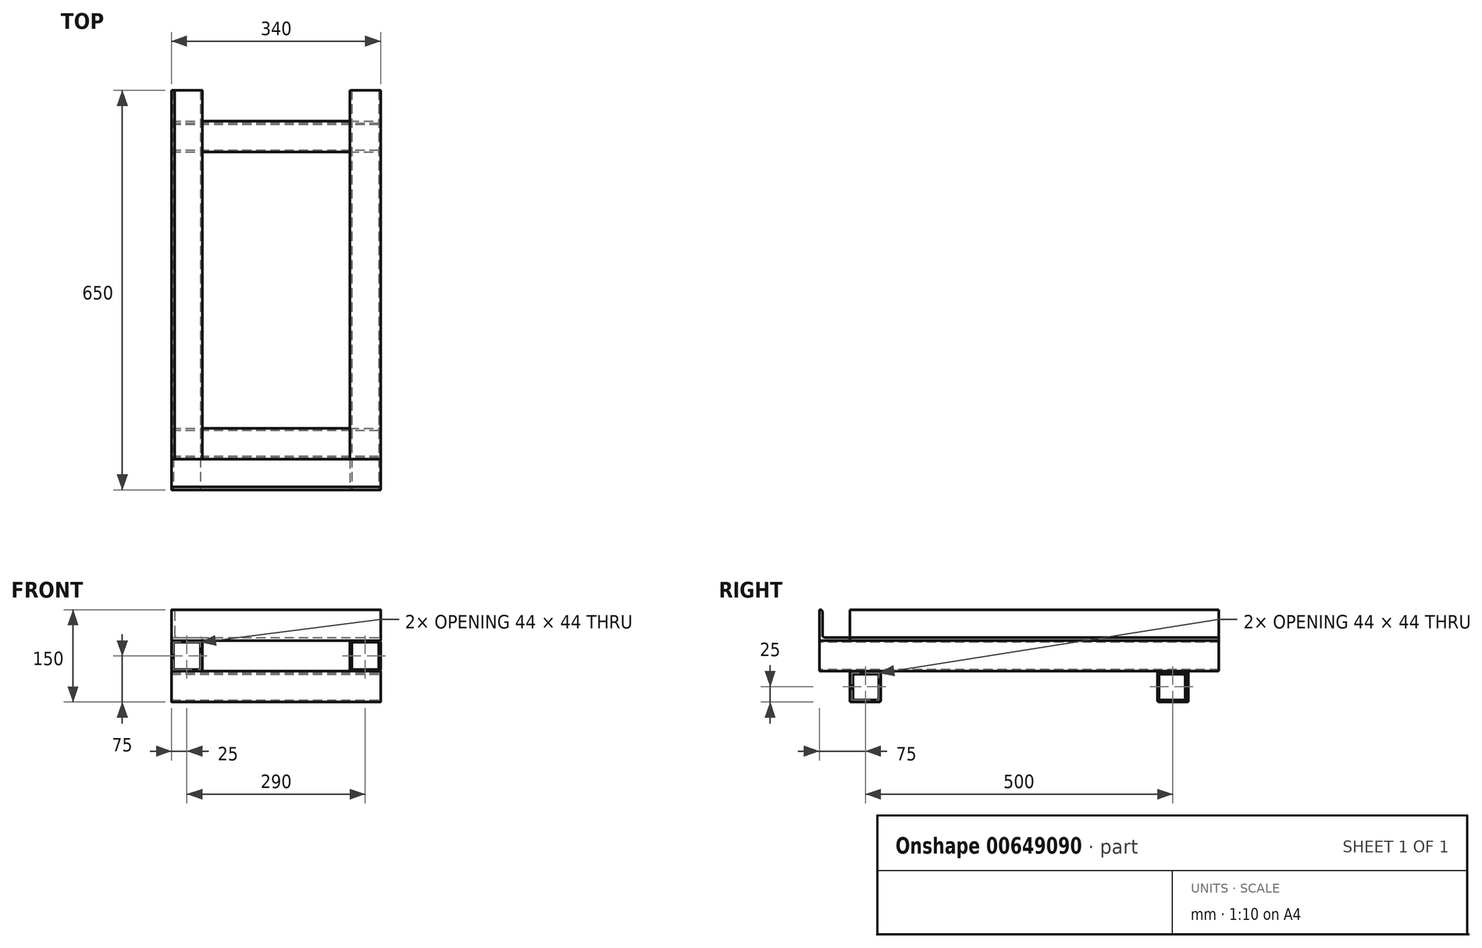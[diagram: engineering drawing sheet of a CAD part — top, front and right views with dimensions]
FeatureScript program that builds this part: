
annotation { "Feature Type Name" : "Feature", "Feature Type Description" : "" }
export const myFeature = defineFeature(function(context is Context, id is Id, definition is map)
    precondition{}
    {
        {
            var Q0;
            Q0=qCreatedBy(makeId("Front.planeOp"),FACE);
            cPlane(context, id + "F0", {"entities" : qUnion([Q0]), "cplaneType" : CPlaneType.OFFSET, "offset" : 300 * mm, "width" : 150 * mm, "height" : 150 * mm});
        }
        {
            var Q0;
            Q0=qCreatedBy(id+"F0.planeOp",FACE);
            var sketch = newSketch(context, id + "F1", { "sketchPlane" : qUnion([Q0])});
            skLineSegment(sketch, "E0.bottom", {"start": v(-167, 250) * mm, "end": v(-123, 250) * mm});
            skLineSegment(sketch, "E0.top", {"start": v(-167, 200) * mm, "end": v(-123, 200) * mm});
            skLineSegment(sketch, "E0.left", {"start": v(-170, 247) * mm, "end": v(-170, 203) * mm});
            skLineSegment(sketch, "E0.right", {"start": v(-120, 247) * mm, "end": v(-120, 203) * mm});
            skLineSegment(sketch, "E1.bottom", {"start": v(123, 250) * mm, "end": v(167, 250) * mm});
            skLineSegment(sketch, "E1.top", {"start": v(123, 200) * mm, "end": v(167, 200) * mm});
            skLineSegment(sketch, "E1.left", {"start": v(120, 247) * mm, "end": v(120, 203) * mm});
            skLineSegment(sketch, "E1.right", {"start": v(170, 247) * mm, "end": v(170, 203) * mm});
            skLineSegment(sketch, "E2.0", {"start": v(-165.5, 203) * mm, "end": v(-124.5, 203) * mm});
            skLineSegment(sketch, "E2.1", {"start": v(-167, 245.5) * mm, "end": v(-167, 204.5) * mm});
            skLineSegment(sketch, "E2.2", {"start": v(-165.5, 247) * mm, "end": v(-124.5, 247) * mm});
            skLineSegment(sketch, "E2.3", {"start": v(-123, 245.5) * mm, "end": v(-123, 204.5) * mm});
            skLineSegment(sketch, "E3.0", {"start": v(124.5, 203) * mm, "end": v(165.5, 203) * mm});
            skLineSegment(sketch, "E3.1", {"start": v(123, 245.5) * mm, "end": v(123, 204.5) * mm});
            skLineSegment(sketch, "E3.2", {"start": v(124.5, 247) * mm, "end": v(165.5, 247) * mm});
            skLineSegment(sketch, "E3.3", {"start": v(167, 245.5) * mm, "end": v(167, 204.5) * mm});
            skPoint(sketch, "E4.visualSharp", {"position": v(-170, 250) * mm});
            skArc(sketch, "E4.filletArc", {"start": v(-167, 250) * mm, "mid": v(-169.12, 249.12) * mm, "end": v(-170, 247) * mm});
            skPoint(sketch, "E5.visualSharp", {"position": v(-120, 250) * mm});
            skArc(sketch, "E5.filletArc", {"start": v(-120, 247) * mm, "mid": v(-120.88, 249.12) * mm, "end": v(-123, 250) * mm});
            skPoint(sketch, "E6.visualSharp", {"position": v(-120, 200) * mm});
            skArc(sketch, "E6.filletArc", {"start": v(-123, 200) * mm, "mid": v(-120.88, 200.88) * mm, "end": v(-120, 203) * mm});
            skPoint(sketch, "E7.visualSharp", {"position": v(-170, 200) * mm});
            skArc(sketch, "E7.filletArc", {"start": v(-170, 203) * mm, "mid": v(-169.12, 200.88) * mm, "end": v(-167, 200) * mm});
            skPoint(sketch, "E8.visualSharp", {"position": v(120, 250) * mm});
            skArc(sketch, "E8.filletArc", {"start": v(123, 250) * mm, "mid": v(120.88, 249.12) * mm, "end": v(120, 247) * mm});
            skPoint(sketch, "E9.visualSharp", {"position": v(170, 250) * mm});
            skArc(sketch, "E9.filletArc", {"start": v(170, 247) * mm, "mid": v(169.12, 249.12) * mm, "end": v(167, 250) * mm});
            skPoint(sketch, "E10.visualSharp", {"position": v(170, 200) * mm});
            skArc(sketch, "E10.filletArc", {"start": v(167, 200) * mm, "mid": v(169.12, 200.88) * mm, "end": v(170, 203) * mm});
            skPoint(sketch, "E11.visualSharp", {"position": v(120, 200) * mm});
            skArc(sketch, "E11.filletArc", {"start": v(120, 203) * mm, "mid": v(120.88, 200.88) * mm, "end": v(123, 200) * mm});
            skArc(sketch, "E12.filletArc", {"start": v(-165.5, 247) * mm, "mid": v(-166.56, 246.56) * mm, "end": v(-167, 245.5) * mm});
            skArc(sketch, "E13.filletArc", {"start": v(-123, 245.5) * mm, "mid": v(-123.44, 246.56) * mm, "end": v(-124.5, 247) * mm});
            skArc(sketch, "E14.filletArc", {"start": v(-124.5, 203) * mm, "mid": v(-123.44, 203.44) * mm, "end": v(-123, 204.5) * mm});
            skArc(sketch, "E15.filletArc", {"start": v(-167, 204.5) * mm, "mid": v(-166.56, 203.44) * mm, "end": v(-165.5, 203) * mm});
            skArc(sketch, "E16.filletArc", {"start": v(124.5, 247) * mm, "mid": v(123.44, 246.56) * mm, "end": v(123, 245.5) * mm});
            skArc(sketch, "E17.filletArc", {"start": v(167, 245.5) * mm, "mid": v(166.56, 246.56) * mm, "end": v(165.5, 247) * mm});
            skArc(sketch, "E18.filletArc", {"start": v(165.5, 203) * mm, "mid": v(166.56, 203.44) * mm, "end": v(167, 204.5) * mm});
            skArc(sketch, "E19.filletArc", {"start": v(123, 204.5) * mm, "mid": v(123.44, 203.44) * mm, "end": v(124.5, 203) * mm});
            skSolve(sketch);
        }
        {
            var Q0;
            Q0=makeQuery(id+"F1.imprint","IMPRINT",FACE,{"disambiguationData":[TD([[makeQuery(id+"F1.imprint","IMPRINT",EDGE,{"derivedFrom":sQuery(id+"F1.wireOp",EDGE,"E0.bottom")}),-1.0]])]});
            var Q1;
            Q1=makeQuery(id+"F1.imprint","IMPRINT",FACE,{"disambiguationData":[TD([[makeQuery(id+"F1.imprint","IMPRINT",EDGE,{"derivedFrom":sQuery(id+"F1.wireOp",EDGE,"E1.bottom")}),-1.0]])]});
            extrude(context, id + "F2", {"entities" : qUnion([Q0, Q1]), "oppositeDirection" : true, "depth" : 650 * mm, "offsetDistance" : 25 * mm});
        }
        {
            var Q0;
            Q0=qCreatedBy(makeId("Front.planeOp"),FACE);
            cPlane(context, id + "F3", {"entities" : qUnion([Q0]), "cplaneType" : CPlaneType.OFFSET, "offset" : 250 * mm, "width" : 150 * mm, "height" : 150 * mm});
        }
        {
            var Q0;
            Q0=qCreatedBy(id+"F3.planeOp",FACE);
            var sketch = newSketch(context, id + "F4", { "sketchPlane" : qUnion([Q0])});
            skLineSegment(sketch, "E20.bottom", {"start": v(-169, 300) * mm, "end": v(-168, 300) * mm});
            skLineSegment(sketch, "E20.left", {"start": v(-170, 299) * mm, "end": v(-170, 251) * mm});
            skLineSegment(sketch, "E21.bottom", {"start": v(-169, 250) * mm, "end": v(-121, 250) * mm});
            skLineSegment(sketch, "E21.top", {"start": v(-161, 255) * mm, "end": v(-123, 255) * mm});
            skLineSegment(sketch, "E21.right", {"start": v(-120, 251) * mm, "end": v(-120, 252) * mm});
            skLineSegment(sketch, "E22", {"start": v(-165, 297) * mm, "end": v(-165, 259) * mm});
            skArc(sketch, "E23.filletArc", {"start": v(-170, 251) * mm, "mid": v(-169.7, 250.3) * mm, "end": v(-169, 250) * mm});
            skArc(sketch, "E24.filletArc", {"start": v(-165, 259) * mm, "mid": v(-163.83, 256.17) * mm, "end": v(-161, 255) * mm});
            skArc(sketch, "E25.filletArc", {"start": v(-169, 300) * mm, "mid": v(-169.7, 299.7) * mm, "end": v(-170, 299) * mm});
            skArc(sketch, "E26.filletArc", {"start": v(-165, 297) * mm, "mid": v(-165.88, 299.12) * mm, "end": v(-168, 300) * mm});
            skArc(sketch, "E27.filletArc", {"start": v(-120, 252) * mm, "mid": v(-120.88, 254.12) * mm, "end": v(-123, 255) * mm});
            skArc(sketch, "E28.filletArc", {"start": v(-121, 250) * mm, "mid": v(-120.3, 250.3) * mm, "end": v(-120, 251) * mm});
            skArc(sketch, "E29.MirrorCS", {"start": v(170, 251) * mm, "mid": v(169.7, 250.3) * mm, "end": v(169, 250) * mm});
            skLineSegment(sketch, "E30.MirrorCS", {"start": v(169, 300) * mm, "end": v(168, 300) * mm});
            skLineSegment(sketch, "E31.MirrorCS", {"start": v(120, 251) * mm, "end": v(120, 252) * mm});
            skArc(sketch, "E32.MirrorCS", {"start": v(121, 250) * mm, "mid": v(120.3, 250.3) * mm, "end": v(120, 251) * mm});
            skArc(sketch, "E33.MirrorCS", {"start": v(169, 300) * mm, "mid": v(169.7, 299.7) * mm, "end": v(170, 299) * mm});
            skArc(sketch, "E34.MirrorCS", {"start": v(120, 252) * mm, "mid": v(120.88, 254.12) * mm, "end": v(123, 255) * mm});
            skArc(sketch, "E35.MirrorCS", {"start": v(165, 297) * mm, "mid": v(165.88, 299.12) * mm, "end": v(168, 300) * mm});
            skArc(sketch, "E36.MirrorCS", {"start": v(165, 259) * mm, "mid": v(163.83, 256.17) * mm, "end": v(161, 255) * mm});
            skLineSegment(sketch, "E37.MirrorCS", {"start": v(165, 297) * mm, "end": v(165, 259) * mm});
            skLineSegment(sketch, "E38.MirrorCS", {"start": v(169, 250) * mm, "end": v(121, 250) * mm});
            skLineSegment(sketch, "E39.MirrorCS", {"start": v(170, 299) * mm, "end": v(170, 251) * mm});
            skLineSegment(sketch, "E40.MirrorCS", {"start": v(161, 255) * mm, "end": v(123, 255) * mm});
            skSolve(sketch);
        }
        {
            var Q0;
            Q0=makeQuery(id+"F4.imprint","IMPRINT",FACE,{"disambiguationData":[TD([[makeQuery(id+"F4.imprint","IMPRINT",EDGE,{"derivedFrom":sQuery(id+"F4.wireOp",EDGE,"E20.bottom")}),-1.0]])]});
            var Q1;
            Q1=makeQuery(id+"F4.imprint","IMPRINT",FACE,{"disambiguationData":[TD([[makeQuery(id+"F4.imprint","IMPRINT",EDGE,{"derivedFrom":sQuery(id+"F4.wireOp",EDGE,"E29.MirrorCS")}),-1.0]])]});
            extrude(context, id + "F5", {"entities" : qUnion([Q0, Q1]), "oppositeDirection" : true, "depth" : 600 * mm, "offsetDistance" : 25 * mm});
        }
        {
            var Q0;
            Q0=qCreatedBy(makeId("Right.planeOp"),FACE);
            cPlane(context, id + "F6", {"entities" : qUnion([Q0]), "cplaneType" : CPlaneType.OFFSET, "offset" : 170 * mm, "width" : 150 * mm, "height" : 150 * mm});
        }
        {
            var Q0;
            Q0=qCreatedBy(id+"F6.planeOp",FACE);
            var sketch = newSketch(context, id + "F7", { "sketchPlane" : qUnion([Q0])});
            skLineSegment(sketch, "E41", {"start": v(-300, 299) * mm, "end": v(-300, 251) * mm});
            skLineSegment(sketch, "E42", {"start": v(-299, 250) * mm, "end": v(-251, 250) * mm});
            skLineSegment(sketch, "E43", {"start": v(-250, 251) * mm, "end": v(-250, 252) * mm});
            skLineSegment(sketch, "E44", {"start": v(-253, 255) * mm, "end": v(-291, 255) * mm});
            skLineSegment(sketch, "E45", {"start": v(-295, 259) * mm, "end": v(-295, 297) * mm});
            skLineSegment(sketch, "E46", {"start": v(-298, 300) * mm, "end": v(-299, 300) * mm});
            skPoint(sketch, "E47.visualSharp", {"position": v(-300, 250) * mm});
            skArc(sketch, "E47.filletArc", {"start": v(-300, 251) * mm, "mid": v(-299.7, 250.3) * mm, "end": v(-299, 250) * mm});
            skPoint(sketch, "E48.visualSharp", {"position": v(-295, 255) * mm});
            skArc(sketch, "E48.filletArc", {"start": v(-295, 259) * mm, "mid": v(-293.83, 256.17) * mm, "end": v(-291, 255) * mm});
            skPoint(sketch, "E49.visualSharp", {"position": v(-300, 300) * mm});
            skArc(sketch, "E49.filletArc", {"start": v(-299, 300) * mm, "mid": v(-299.7, 299.7) * mm, "end": v(-300, 299) * mm});
            skPoint(sketch, "E50.visualSharp", {"position": v(-295, 300) * mm});
            skArc(sketch, "E50.filletArc", {"start": v(-295, 297) * mm, "mid": v(-295.88, 299.12) * mm, "end": v(-298, 300) * mm});
            skPoint(sketch, "E51.visualSharp", {"position": v(-250, 255) * mm});
            skArc(sketch, "E51.filletArc", {"start": v(-250, 252) * mm, "mid": v(-250.88, 254.12) * mm, "end": v(-253, 255) * mm});
            skPoint(sketch, "E52.visualSharp", {"position": v(-250, 250) * mm});
            skArc(sketch, "E52.filletArc", {"start": v(-251, 250) * mm, "mid": v(-250.3, 250.3) * mm, "end": v(-250, 251) * mm});
            skSolve(sketch);
        }
        {
            var Q0;
            Q0=makeQuery(id+"F7.imprint","IMPRINT",FACE,{"disambiguationData":[TD([[makeQuery(id+"F7.imprint","IMPRINT",EDGE,{"derivedFrom":sQuery(id+"F7.wireOp",EDGE,"E41")}),1.0]])]});
            extrude(context, id + "F8", {"entities" : qUnion([Q0]), "oppositeDirection" : true, "depth" : 340 * mm, "offsetDistance" : 25 * mm});
        }
        {
            var Q0;
            Q0=qCreatedBy(id+"F6.planeOp",FACE);
            var sketch = newSketch(context, id + "F9", { "sketchPlane" : qUnion([Q0])});
            skLineSegment(sketch, "E53.bottom", {"start": v(-247, 200) * mm, "end": v(-203, 200) * mm});
            skLineSegment(sketch, "E53.top", {"start": v(-247, 150) * mm, "end": v(-203, 150) * mm});
            skLineSegment(sketch, "E53.left", {"start": v(-250, 197) * mm, "end": v(-250, 153) * mm});
            skLineSegment(sketch, "E53.right", {"start": v(-200, 197) * mm, "end": v(-200, 153) * mm});
            skLineSegment(sketch, "E54.bottom", {"start": v(253, 200) * mm, "end": v(297, 200) * mm});
            skLineSegment(sketch, "E54.top", {"start": v(253, 150) * mm, "end": v(297, 150) * mm});
            skLineSegment(sketch, "E54.left", {"start": v(250, 197) * mm, "end": v(250, 153) * mm});
            skLineSegment(sketch, "E54.right", {"start": v(300, 197) * mm, "end": v(300, 153) * mm});
            skLineSegment(sketch, "E55.0", {"start": v(-203, 195.5) * mm, "end": v(-203, 154.5) * mm});
            skLineSegment(sketch, "E55.1", {"start": v(-245.5, 197) * mm, "end": v(-204.5, 197) * mm});
            skLineSegment(sketch, "E55.2", {"start": v(-247, 195.5) * mm, "end": v(-247, 154.5) * mm});
            skLineSegment(sketch, "E55.3", {"start": v(-245.5, 153) * mm, "end": v(-204.5, 153) * mm});
            skLineSegment(sketch, "E56.0", {"start": v(254.5, 197) * mm, "end": v(295.5, 197) * mm});
            skLineSegment(sketch, "E56.1", {"start": v(253, 195.5) * mm, "end": v(253, 154.5) * mm});
            skLineSegment(sketch, "E56.2", {"start": v(254.5, 153) * mm, "end": v(295.5, 153) * mm});
            skLineSegment(sketch, "E56.3", {"start": v(297, 195.5) * mm, "end": v(297, 154.5) * mm});
            skPoint(sketch, "E57.visualSharp", {"position": v(-250, 200) * mm});
            skArc(sketch, "E57.filletArc", {"start": v(-247, 200) * mm, "mid": v(-249.12, 199.12) * mm, "end": v(-250, 197) * mm});
            skPoint(sketch, "E58.visualSharp", {"position": v(-200, 200) * mm});
            skArc(sketch, "E58.filletArc", {"start": v(-200, 197) * mm, "mid": v(-200.88, 199.12) * mm, "end": v(-203, 200) * mm});
            skPoint(sketch, "E59.visualSharp", {"position": v(-200, 150) * mm});
            skArc(sketch, "E59.filletArc", {"start": v(-203, 150) * mm, "mid": v(-200.88, 150.88) * mm, "end": v(-200, 153) * mm});
            skPoint(sketch, "E60.visualSharp", {"position": v(-250, 150) * mm});
            skArc(sketch, "E60.filletArc", {"start": v(-250, 153) * mm, "mid": v(-249.12, 150.88) * mm, "end": v(-247, 150) * mm});
            skPoint(sketch, "E61.visualSharp", {"position": v(250, 200) * mm});
            skArc(sketch, "E61.filletArc", {"start": v(253, 200) * mm, "mid": v(250.88, 199.12) * mm, "end": v(250, 197) * mm});
            skPoint(sketch, "E62.visualSharp", {"position": v(300, 200) * mm});
            skArc(sketch, "E62.filletArc", {"start": v(300, 197) * mm, "mid": v(299.12, 199.12) * mm, "end": v(297, 200) * mm});
            skPoint(sketch, "E63.visualSharp", {"position": v(300, 150) * mm});
            skArc(sketch, "E63.filletArc", {"start": v(297, 150) * mm, "mid": v(299.12, 150.88) * mm, "end": v(300, 153) * mm});
            skPoint(sketch, "E64.visualSharp", {"position": v(250, 150) * mm});
            skArc(sketch, "E64.filletArc", {"start": v(250, 153) * mm, "mid": v(250.88, 150.88) * mm, "end": v(253, 150) * mm});
            skArc(sketch, "E65.filletArc", {"start": v(254.5, 197) * mm, "mid": v(253.44, 196.56) * mm, "end": v(253, 195.5) * mm});
            skArc(sketch, "E66.filletArc", {"start": v(297, 195.5) * mm, "mid": v(296.56, 196.56) * mm, "end": v(295.5, 197) * mm});
            skArc(sketch, "E67.filletArc", {"start": v(295.5, 153) * mm, "mid": v(296.56, 153.44) * mm, "end": v(297, 154.5) * mm});
            skArc(sketch, "E68.filletArc", {"start": v(253, 154.5) * mm, "mid": v(253.44, 153.44) * mm, "end": v(254.5, 153) * mm});
            skArc(sketch, "E69.filletArc", {"start": v(-245.5, 197) * mm, "mid": v(-246.56, 196.56) * mm, "end": v(-247, 195.5) * mm});
            skArc(sketch, "E70.filletArc", {"start": v(-203, 195.5) * mm, "mid": v(-203.44, 196.56) * mm, "end": v(-204.5, 197) * mm});
            skArc(sketch, "E71.filletArc", {"start": v(-204.5, 153) * mm, "mid": v(-203.44, 153.44) * mm, "end": v(-203, 154.5) * mm});
            skArc(sketch, "E72.filletArc", {"start": v(-247, 154.5) * mm, "mid": v(-246.56, 153.44) * mm, "end": v(-245.5, 153) * mm});
            skSolve(sketch);
        }
        {
            var Q0;
            Q0=makeQuery(id+"F9.imprint","IMPRINT",FACE,{"disambiguationData":[TD([[makeQuery(id+"F9.imprint","IMPRINT",EDGE,{"derivedFrom":sQuery(id+"F9.wireOp",EDGE,"E53.bottom")}),-1.0]])]});
            var Q1;
            Q1=makeQuery(id+"F9.imprint","IMPRINT",FACE,{"disambiguationData":[TD([[makeQuery(id+"F9.imprint","IMPRINT",EDGE,{"derivedFrom":sQuery(id+"F9.wireOp",EDGE,"E54.bottom")}),-1.0]])]});
            extrude(context, id + "F10", {"entities" : qUnion([Q0, Q1]), "oppositeDirection" : true, "depth" : 340 * mm, "offsetDistance" : 25 * mm});
        }
        {
            var Q0;
            Q0=qCreatedBy(id+"F6.planeOp",FACE);
            var sketch = newSketch(context, id + "F11", { "sketchPlane" : qUnion([Q0])});
            skLineSegment(sketch, "E73", {"start": v(-200, 199) * mm, "end": v(-200, 198) * mm});
            skLineSegment(sketch, "E74", {"start": v(-242, 195) * mm, "end": v(-203, 195) * mm});
            skLineSegment(sketch, "E75", {"start": v(-245, 153) * mm, "end": v(-245, 192) * mm});
            skLineSegment(sketch, "E76", {"start": v(-249, 200) * mm, "end": v(-201, 200) * mm});
            skLineSegment(sketch, "E77", {"start": v(-250, 199) * mm, "end": v(-250, 151) * mm});
            skLineSegment(sketch, "E78", {"start": v(-248, 150) * mm, "end": v(-249, 150) * mm});
            skLineSegment(sketch, "E79", {"start": v(250, 199) * mm, "end": v(250, 198) * mm});
            skLineSegment(sketch, "E80", {"start": v(253, 195) * mm, "end": v(292, 195) * mm});
            skLineSegment(sketch, "E81", {"start": v(295, 192) * mm, "end": v(295, 153) * mm});
            skLineSegment(sketch, "E82", {"start": v(298, 150) * mm, "end": v(299, 150) * mm});
            skLineSegment(sketch, "E83", {"start": v(300, 151) * mm, "end": v(300, 199) * mm});
            skLineSegment(sketch, "E84", {"start": v(299, 200) * mm, "end": v(251, 200) * mm});
            skPoint(sketch, "E85.visualSharp", {"position": v(-250, 200) * mm});
            skArc(sketch, "E85.filletArc", {"start": v(-249, 200) * mm, "mid": v(-249.7, 199.7) * mm, "end": v(-250, 199) * mm});
            skPoint(sketch, "E86.visualSharp", {"position": v(-250, 150) * mm});
            skArc(sketch, "E86.filletArc", {"start": v(-250, 151) * mm, "mid": v(-249.7, 150.3) * mm, "end": v(-249, 150) * mm});
            skPoint(sketch, "E87.visualSharp", {"position": v(-200, 200) * mm});
            skArc(sketch, "E87.filletArc", {"start": v(-200, 199) * mm, "mid": v(-200.3, 199.7) * mm, "end": v(-201, 200) * mm});
            skPoint(sketch, "E88.visualSharp", {"position": v(-245, 150) * mm});
            skArc(sketch, "E88.filletArc", {"start": v(-248, 150) * mm, "mid": v(-245.88, 150.88) * mm, "end": v(-245, 153) * mm});
            skPoint(sketch, "E89.visualSharp", {"position": v(-200, 195) * mm});
            skArc(sketch, "E89.filletArc", {"start": v(-203, 195) * mm, "mid": v(-200.88, 195.88) * mm, "end": v(-200, 198) * mm});
            skPoint(sketch, "E90.visualSharp", {"position": v(-245, 195) * mm});
            skArc(sketch, "E90.filletArc", {"start": v(-242, 195) * mm, "mid": v(-244.12, 194.12) * mm, "end": v(-245, 192) * mm});
            skPoint(sketch, "E91.visualSharp", {"position": v(250, 195) * mm});
            skArc(sketch, "E91.filletArc", {"start": v(250, 198) * mm, "mid": v(250.88, 195.88) * mm, "end": v(253, 195) * mm});
            skPoint(sketch, "E92.visualSharp", {"position": v(295, 195) * mm});
            skArc(sketch, "E92.filletArc", {"start": v(295, 192) * mm, "mid": v(294.12, 194.12) * mm, "end": v(292, 195) * mm});
            skPoint(sketch, "E93.visualSharp", {"position": v(295, 150) * mm});
            skArc(sketch, "E93.filletArc", {"start": v(295, 153) * mm, "mid": v(295.88, 150.88) * mm, "end": v(298, 150) * mm});
            skPoint(sketch, "E94.visualSharp", {"position": v(300, 150) * mm});
            skArc(sketch, "E94.filletArc", {"start": v(299, 150) * mm, "mid": v(299.7, 150.3) * mm, "end": v(300, 151) * mm});
            skPoint(sketch, "E95.visualSharp", {"position": v(300, 200) * mm});
            skArc(sketch, "E95.filletArc", {"start": v(300, 199) * mm, "mid": v(299.7, 199.7) * mm, "end": v(299, 200) * mm});
            skPoint(sketch, "E96.visualSharp", {"position": v(250, 200) * mm});
            skArc(sketch, "E96.filletArc", {"start": v(251, 200) * mm, "mid": v(250.3, 199.7) * mm, "end": v(250, 199) * mm});
            skSolve(sketch);
        }
        {
            var Q0;
            Q0=makeQuery(id+"F11.imprint","IMPRINT",FACE,{"disambiguationData":[TD([[makeQuery(id+"F11.imprint","IMPRINT",EDGE,{"derivedFrom":sQuery(id+"F11.wireOp",EDGE,"E73")}),-1.0]])]});
            var Q1;
            Q1=makeQuery(id+"F11.imprint","IMPRINT",FACE,{"disambiguationData":[TD([[makeQuery(id+"F11.imprint","IMPRINT",EDGE,{"derivedFrom":sQuery(id+"F11.wireOp",EDGE,"E79")}),1.0]])]});
            extrude(context, id + "F12", {"entities" : qUnion([Q0, Q1]), "oppositeDirection" : true, "depth" : 340 * mm, "offsetDistance" : 25 * mm});
        }
    });
